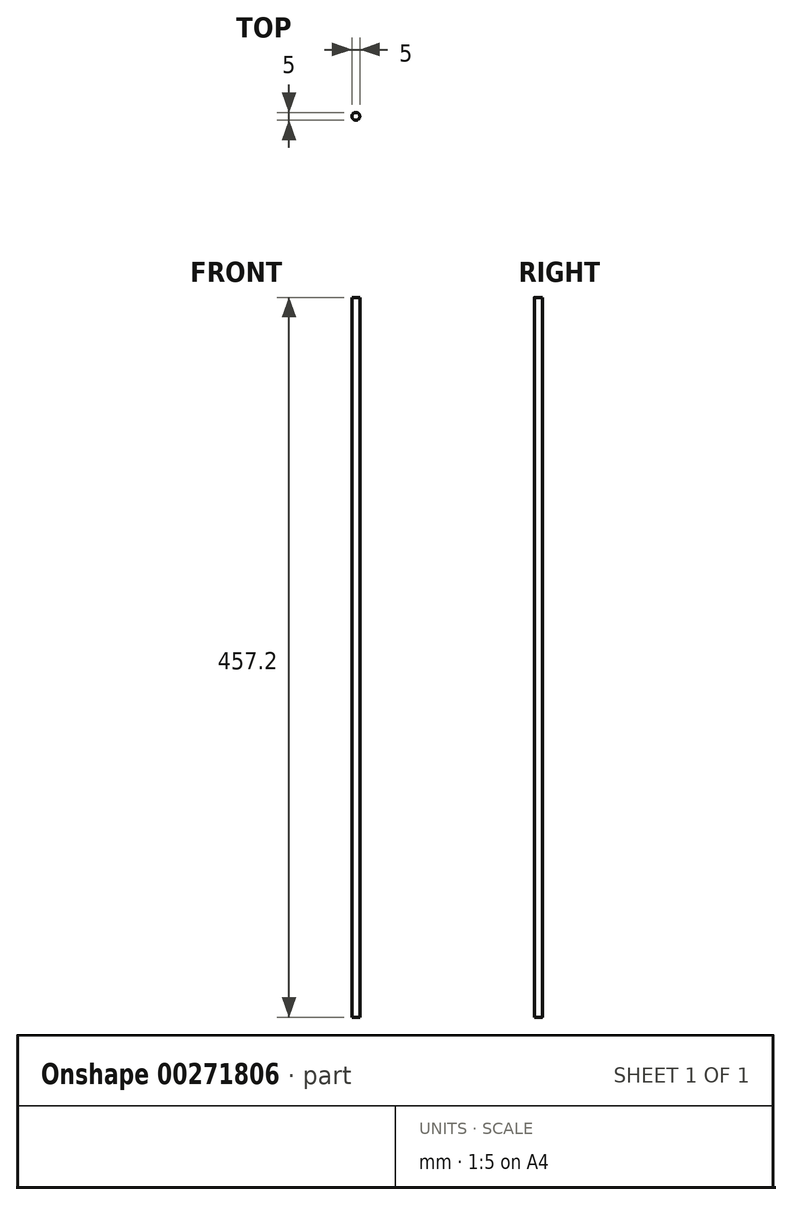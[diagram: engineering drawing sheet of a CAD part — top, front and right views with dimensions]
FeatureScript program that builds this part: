
annotation { "Feature Type Name" : "Feature", "Feature Type Description" : "" }
export const myFeature = defineFeature(function(context is Context, id is Id, definition is map)
    precondition{}
    {
        {
            var Q0;
            Q0=qCreatedBy(makeId("Top.planeOp"),FACE);
            var sketch = newSketch(context, id + "F0", { "sketchPlane" : qUnion([Q0])});
            skCircle(sketch, "E0", {"center": v(0, 0) * mm, "radius": 2.5 * mm});
            skSolve(sketch);
        }
        {
            var Q0;
            Q0 = qSketchRegion(id + "F0", true);
            extrude(context, id + "F1", {"entities" : qUnion([Q0]), "depth" : 457.2 * mm});
        }
    });
